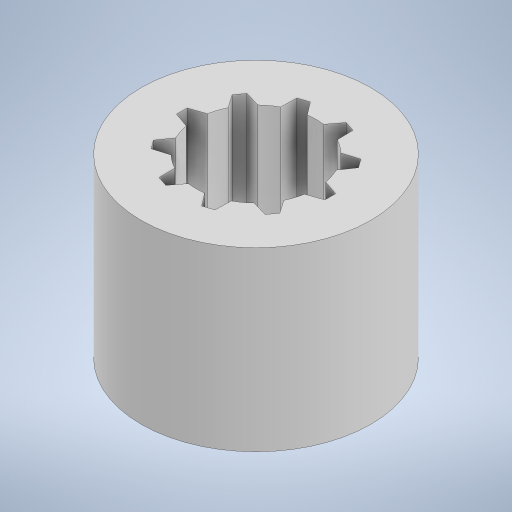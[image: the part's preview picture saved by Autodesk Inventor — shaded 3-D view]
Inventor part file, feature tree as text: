
AUTODESK INVENTOR PART (.ipt)
format: ipt  version: 2024 (Build 280153000, 153)  size: 561,152 bytes
history: native  units: in
note: dims shown in document units (in); Inventor stores cm internally (conversion verified against a paired STEP export)
features: extrude x8, sketch x7, projected_geometry x6
ambient origin geometry x8: Origin, YZ Plane, XZ Plane, XY Plane, X Axis, Y Axis, Z Axis, Center Point
bodies: Solid1 (feature_tree)
feature tree (21):
  extrude  "Extrusion1"  Depth=0.1181in
  extrude  "Extrusion2"  Depth=0.1575in
  extrude  "Extrusion3"  Depth=0.7515in
  extrude  "Extrusion4"  Depth=3.937in TaperAngle=0.0deg
  extrude  "Extrusion5"  Depth=0.315in
  extrude  "Extrusion6"  Depth=17.685in TaperAngle=0.0deg
  extrude  "Extrusion7"  Depth=1.9685in
  extrude  "Extrusion8"  Depth=1.9685in TaperAngle=0.0deg
  sketch  "Sketch2"  dims[d0=1.3386in d1=0.1181in]
  projected_geometry  "Projected Loop1"
  sketch  "Sketch3"  dims[d2=0.2362in d3=0.1575in]
  sketch  "Sketch4"  dims[d4=0.7515in d5=0.7515in]
  projected_geometry  "Projected Loop2"
  sketch  "Sketch5"  dims[d6=3.937in d8=360.0deg d10=0.1969in d11=0.0in]
  projected_geometry  "Projected Loop3"
  sketch  "Sketch6"  dims[d12=19.685in d13=0.0in d14=0.315in]
  projected_geometry  "Projected Loop4"
  sketch  "Sketch7"  dims[d15=20.815in d16=0.0in d17=17.685in d18=0.0in]
  projected_geometry  "Projected Loop5"
  sketch  "Sketch8"  dims[d19=0.2283in d20=0.0in d21=3.5433in d22=1.9685in d23=0.0in d24=2.5591in d25=2.969in d26=0.0in d27=2.969in d28=0.0in]
  projected_geometry  "Projected Loop6"
